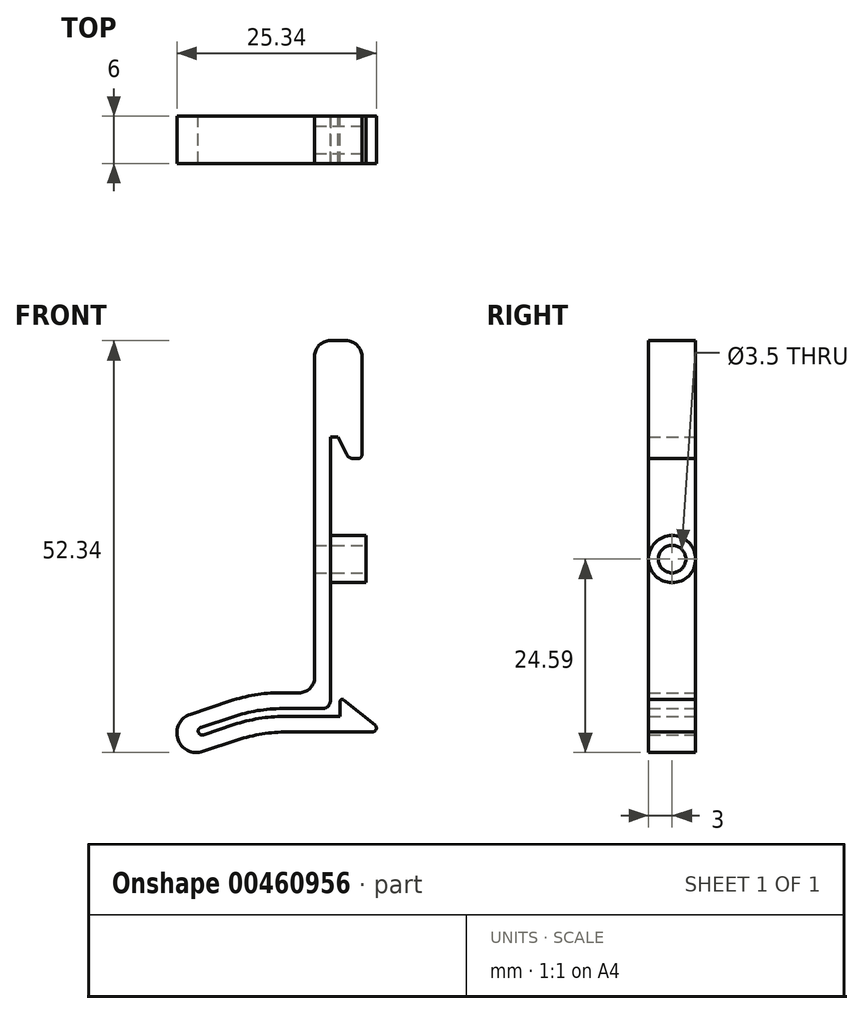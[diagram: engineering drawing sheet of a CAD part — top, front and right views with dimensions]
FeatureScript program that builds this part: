
annotation { "Feature Type Name" : "Feature", "Feature Type Description" : "" }
export const myFeature = defineFeature(function(context is Context, id is Id, definition is map)
    precondition{}
    {
        {
            var Q0;
            Q0=qCreatedBy(makeId("Front.planeOp"),FACE);
            var sketch = newSketch(context, id + "F0", { "sketchPlane" : qUnion([Q0])});
            skLineSegment(sketch, "E0", {"start": v(14.5, 14) * mm, "end": v(14.5, 10) * mm});
            skArc(sketch, "E1", {"start": v(18, 11.5) * mm, "mid": v(18.35, 11.65) * mm, "end": v(18.5, 12) * mm});
            skArc(sketch, "E2", {"start": v(18.5, 24.5) * mm, "mid": v(17.91, 25.91) * mm, "end": v(16.5, 26.5) * mm});
            skLineSegment(sketch, "E3", {"start": v(18.5, 24.5) * mm, "end": v(18.5, 12) * mm});
            skLineSegment(sketch, "E4", {"start": v(14.5, 14.25) * mm, "end": v(15.5, 14.25) * mm});
            skLineSegment(sketch, "E5", {"start": v(15.75, -21.25) * mm, "end": v(15.75, -19.32) * mm});
            skArc(sketch, "E6", {"start": v(16.15, -19.12) * mm, "mid": v(15.9, -19.1) * mm, "end": v(15.75, -19.32) * mm});
            skLineSegment(sketch, "E7", {"start": v(14.5, -19.25) * mm, "end": v(14.5, 14.25) * mm});
            skArc(sketch, "E8", {"start": v(9.03, -23.21) * mm, "mid": v(5.83, -23.47) * mm, "end": v(2.7, -24.24) * mm});
            skArc(sketch, "E9", {"start": v(8.6, -21.25) * mm, "mid": v(5.39, -21.5) * mm, "end": v(2.27, -22.28) * mm});
            skArc(sketch, "E10", {"start": v(8.43, -20.25) * mm, "mid": v(5.23, -20.5) * mm, "end": v(2.1, -21.28) * mm});
            skArc(sketch, "E11", {"start": v(-1.95, -22.63) * mm, "mid": v(-2.26, -23.26) * mm, "end": v(-1.63, -23.58) * mm});
            skArc(sketch, "E12", {"start": v(13.5, -20.25) * mm, "mid": v(14.2, -19.96) * mm, "end": v(14.5, -19.25) * mm});
            skLineSegment(sketch, "E13", {"start": v(15.75, -21.25) * mm, "end": v(8.6, -21.25) * mm});
            skLineSegment(sketch, "E14", {"start": v(2.27, -22.28) * mm, "end": v(-1.63, -23.58) * mm});
            skLineSegment(sketch, "E15", {"start": v(13.5, -20.25) * mm, "end": v(8.43, -20.25) * mm});
            skLineSegment(sketch, "E16", {"start": v(2.1, -21.28) * mm, "end": v(-1.95, -22.63) * mm});
            skLineSegment(sketch, "E17", {"start": v(2.7, -24.24) * mm, "end": v(-1.7, -25.71) * mm});
            skLineSegment(sketch, "E18", {"start": v(9.03, -23.21) * mm, "end": v(19.84, -23.21) * mm});
            skLineSegment(sketch, "E19", {"start": v(20.15, -22.32) * mm, "end": v(16.15, -19.12) * mm});
            skArc(sketch, "E20", {"start": v(19.84, -23.21) * mm, "mid": v(20.3, -22.88) * mm, "end": v(20.15, -22.32) * mm});
            skLineSegment(sketch, "E21", {"start": v(15.5, 14.25) * mm, "end": v(16.54, 12.07) * mm});
            skLineSegment(sketch, "E22", {"start": v(17.44, 11.5) * mm, "end": v(18, 11.5) * mm});
            skArc(sketch, "E23", {"start": v(16.54, 12.07) * mm, "mid": v(16.9, 11.65) * mm, "end": v(17.44, 11.5) * mm});
            skArc(sketch, "E24", {"start": v(10.5, -18.25) * mm, "mid": v(11.91, -17.66) * mm, "end": v(12.5, -16.25) * mm});
            skLineSegment(sketch, "E25", {"start": v(12.5, 22.5) * mm, "end": v(12.5, -16.25) * mm});
            skLineSegment(sketch, "E26", {"start": v(10.5, -18.25) * mm, "end": v(8.1, -18.25) * mm});
            skArc(sketch, "E27", {"start": v(8.1, -18.25) * mm, "mid": v(4.9, -18.5) * mm, "end": v(1.78, -19.28) * mm});
            skArc(sketch, "E28", {"start": v(-18, 24.5) * mm, "mid": v(-19.41, 23.91) * mm, "end": v(-20, 22.5) * mm});
            skArc(sketch, "E29", {"start": v(-20, 26.5) * mm, "mid": v(-21.41, 25.91) * mm, "end": v(-22, 24.5) * mm});
            skLineSegment(sketch, "E30", {"start": v(1.78, -19.28) * mm, "end": v(-3.3, -20.97) * mm});
            skArc(sketch, "E31", {"start": v(-3.3, -20.97) * mm, "mid": v(-4.87, -24.13) * mm, "end": v(-1.7, -25.71) * mm});
            skLineSegment(sketch, "E32", {"start": v(12.5, 22.5) * mm, "end": v(12.5, 24.5) * mm});
            skLineSegment(sketch, "E33", {"start": v(16.5, 26.5) * mm, "end": v(14.5, 26.5) * mm});
            skArc(sketch, "E34", {"start": v(14.5, 26.5) * mm, "mid": v(13.08, 25.91) * mm, "end": v(12.5, 24.5) * mm});
            skSolve(sketch);
        }
        {
            var Q0;
            Q0=makeQuery(id+"F0.imprint","IMPRINT",FACE,{"disambiguationData":[TD([[makeQuery(id+"F0.imprint","IMPRINT",EDGE,{"derivedFrom":sQuery(id+"F0.wireOp",EDGE,"E1")}),1.0]])]});
            extrude(context, id + "F1", {"entities" : qUnion([Q0]), "depth" : 6 * mm});
        }
        {
            var Q0;
            Q0=makeQuery(id+"F1.opExtrude","SWEPT_FACE",FACE,{"disambiguationData":[OSD([sQuery(id+"F0.wireOp",EDGE,"E7")])]});
            var sketch = newSketch(context, id + "F2", { "sketchPlane" : qUnion([Q0])});
            skLineSegment(sketch, "E35.0", {"start": v(-6, -16.25) * mm, "end": v(0, -16.25) * mm});
            skCircle(sketch, "E36", {"center": v(-3, -1.25) * mm, "radius": 3 * mm});
            skLineSegment(sketch, "E37.0", {"start": v(0, -19.25) * mm, "end": v(0, 14.25) * mm});
            skSolve(sketch);
        }
        {
            var Q0;
            Q0 = qSketchRegion(id + "F2", true);
            extrude(context, id + "F3", {"entities" : qUnion([Q0]), "operationType" : NewBodyOperationType.ADD, "depth" : 4.5 * mm});
        }
        {
            var Q0;
            Q0=makeQuery(id+"F3.opExtrude","CAP_FACE",FACE,{"disambiguationData":[OSD([sQuery(id+"F2.wireOp",EDGE,"E36")])],"isStart":false});
            var sketch = newSketch(context, id + "F4", { "sketchPlane" : qUnion([Q0])});
            skPoint(sketch, "E38", {"position": v(-3, -1.25) * mm});
            skSolve(sketch);
        }
        {
            var Q0;
            Q0=sQuery(id+"F4.wireOp",VERTEX,"E38");
            var Q1;
            Q1=makeQuery(id+"F1.opExtrude","SWEPT_BODY",BODY,{"disambiguationData":[OSD([sQuery(id+"F0.wireOp",EDGE,"E1"),sQuery(id+"F0.wireOp",EDGE,"E2"),sQuery(id+"F0.wireOp",EDGE,"E3"),sQuery(id+"F0.wireOp",EDGE,"E4"),sQuery(id+"F0.wireOp",EDGE,"E5"),sQuery(id+"F0.wireOp",EDGE,"E6"),sQuery(id+"F0.wireOp",EDGE,"E7"),sQuery(id+"F0.wireOp",EDGE,"E8"),sQuery(id+"F0.wireOp",EDGE,"E9"),sQuery(id+"F0.wireOp",EDGE,"E10"),sQuery(id+"F0.wireOp",EDGE,"E11"),sQuery(id+"F0.wireOp",EDGE,"E12"),sQuery(id+"F0.wireOp",EDGE,"E13"),sQuery(id+"F0.wireOp",EDGE,"E14"),sQuery(id+"F0.wireOp",EDGE,"E15"),sQuery(id+"F0.wireOp",EDGE,"E16"),sQuery(id+"F0.wireOp",EDGE,"E17"),sQuery(id+"F0.wireOp",EDGE,"E18"),sQuery(id+"F0.wireOp",EDGE,"E19"),sQuery(id+"F0.wireOp",EDGE,"E20"),sQuery(id+"F0.wireOp",EDGE,"E21"),sQuery(id+"F0.wireOp",EDGE,"E22"),sQuery(id+"F0.wireOp",EDGE,"E23"),sQuery(id+"F0.wireOp",EDGE,"E24"),sQuery(id+"F0.wireOp",EDGE,"E25"),sQuery(id+"F0.wireOp",EDGE,"E26"),sQuery(id+"F0.wireOp",EDGE,"E27"),sQuery(id+"F0.wireOp",EDGE,"E30"),sQuery(id+"F0.wireOp",EDGE,"E31"),sQuery(id+"F0.wireOp",EDGE,"E32"),sQuery(id+"F0.wireOp",EDGE,"E33"),sQuery(id+"F0.wireOp",EDGE,"E34")])]});
            hole(context, id + "F5", {"style" : HoleStyle.SIMPLE, "endStyle" : HoleEndStyle.THROUGH, "holeDiameter" : 3.5 * mm, "isTappedThrough" : true, "tappedDepth" : 12 * mm, "tapClearance" : 3, "locations" : qUnion([Q0]), "scope" : qUnion([Q1])});
        }
    });
